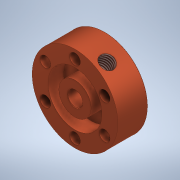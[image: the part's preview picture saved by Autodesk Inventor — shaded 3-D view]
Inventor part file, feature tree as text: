
AUTODESK INVENTOR PART (.ipt)
format: ipt  version: 2020 (Build 240168000, 168)  size: 190,464 bytes
history: native  units: mm
features: sketch x3, hole x2, plane x2, revolve x1, pattern_circular x1, chamfer x1
ambient origin geometry x8: Origin, YZ Plane, XZ Plane, XY Plane, X Axis, Y Axis, Z Axis, Center Point
bodies: Solid1 (feature_tree)
feature tree (10):
  revolve  "Revolution1"  [1 undecoded]
  hole  "Hole1"  [1 undecoded]
  pattern_circular  "Circular Pattern1"  [2 undecoded]
  plane  "Work Plane2"
  hole  "Hole2"  [1 undecoded]
  chamfer  "Chamfer1"  Angle=60.0deg  [1 undecoded]
  sketch  "Sketch1"  dims[d0=7.0mm d1=25.2mm]
  sketch  "Sketch2"  dims[d3=14.0mm d4=40.0mm]
  plane  "Work Plane1"
  sketch  "Sketch3"  dims[d5=90.0deg d6=16.0mm d7=5.0mm d8=6.0mm d9=4.0mm d10=2.0mm d11=90.0deg d12=8.0mm d13=20.594885mm d14=60.0mm d15=360.0deg d17=60.0deg d18=6.647mm d19=8.5mm d20=4.0mm d21=2.0mm d22=90.0deg d23=9.2mm d24=20.594885mm d25=0.2mm d26=2.0mm d27=45.0deg d28=2.0mm d29=4.0mm]
note: 6 required parameter values undecoded (feature->parameter linkage not recoverable at this tier; creation-order binding heuristic only, values carry confidence <= 0.55)